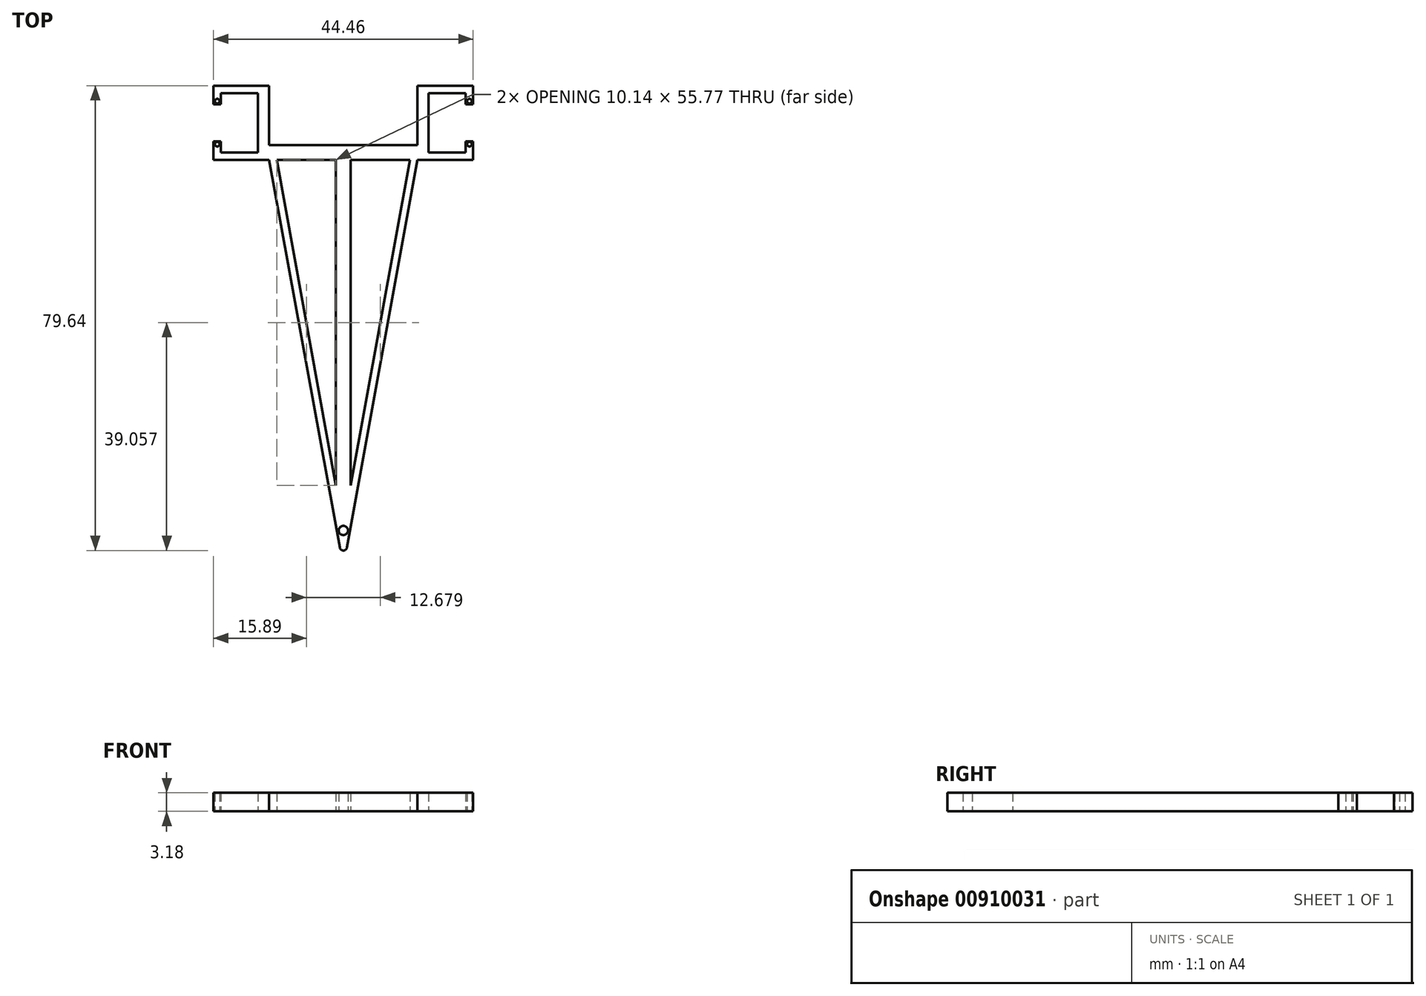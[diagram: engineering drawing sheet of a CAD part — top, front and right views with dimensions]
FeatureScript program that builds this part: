
annotation { "Feature Type Name" : "Feature", "Feature Type Description" : "" }
export const myFeature = defineFeature(function(context is Context, id is Id, definition is map)
    precondition{}
    {
        {
            var Q0;
            Q0=qCreatedBy(makeId("Top.planeOp"),FACE);
            var sketch = newSketch(context, id + "F0", { "sketchPlane" : qUnion([Q0])});
            skLineSegment(sketch, "E0", {"start": v(-22.23, 11.43) * mm, "end": v(-12.7, 11.43) * mm});
            skLineSegment(sketch, "E1", {"start": v(-12.7, 11.43) * mm, "end": v(-12.7, -1.27) * mm});
            skLineSegment(sketch, "E2", {"start": v(-12.7, -1.27) * mm, "end": v(-22.23, -1.27) * mm});
            skLineSegment(sketch, "E3", {"start": v(-22.23, -1.27) * mm, "end": v(-22.23, 1.9) * mm});
            skLineSegment(sketch, "E4", {"start": v(-22.23, 1.9) * mm, "end": v(-20.96, 1.9) * mm});
            skLineSegment(sketch, "E5", {"start": v(-20.96, 1.9) * mm, "end": v(-20.96, 0) * mm});
            skLineSegment(sketch, "E6", {"start": v(-20.96, 0) * mm, "end": v(-14.6, 0) * mm});
            skLineSegment(sketch, "E7", {"start": v(-14.6, 0) * mm, "end": v(-14.6, 10.16) * mm});
            skLineSegment(sketch, "E8", {"start": v(-14.6, 10.16) * mm, "end": v(-20.96, 10.16) * mm});
            skLineSegment(sketch, "E9", {"start": v(-20.96, 10.16) * mm, "end": v(-20.96, 8.26) * mm});
            skLineSegment(sketch, "E10", {"start": v(-20.96, 8.25) * mm, "end": v(-22.23, 8.25) * mm});
            skLineSegment(sketch, "E11", {"start": v(-22.23, 8.26) * mm, "end": v(-22.23, 11.43) * mm});
            skLineSegment(sketch, "E12.MirrorCS", {"start": v(14.6, 0) * mm, "end": v(14.6, 10.16) * mm});
            skLineSegment(sketch, "E13.MirrorCS", {"start": v(12.7, 11.43) * mm, "end": v(12.7, -1.27) * mm});
            skLineSegment(sketch, "E14.MirrorCS", {"start": v(20.96, 0) * mm, "end": v(14.6, 0) * mm});
            skLineSegment(sketch, "E15.MirrorCS", {"start": v(12.7, -1.27) * mm, "end": v(22.23, -1.27) * mm});
            skLineSegment(sketch, "E16.MirrorCS", {"start": v(22.23, -1.27) * mm, "end": v(22.23, 1.9) * mm});
            skLineSegment(sketch, "E17.MirrorCS", {"start": v(20.96, 1.9) * mm, "end": v(20.96, 0) * mm});
            skLineSegment(sketch, "E18.MirrorCS", {"start": v(22.23, 1.9) * mm, "end": v(20.96, 1.9) * mm});
            skLineSegment(sketch, "E19.MirrorCS", {"start": v(20.96, 8.25) * mm, "end": v(22.23, 8.25) * mm});
            skLineSegment(sketch, "E20.MirrorCS", {"start": v(22.23, 8.26) * mm, "end": v(22.23, 11.43) * mm});
            skLineSegment(sketch, "E21.MirrorCS", {"start": v(20.96, 10.16) * mm, "end": v(20.96, 8.26) * mm});
            skLineSegment(sketch, "E22.MirrorCS", {"start": v(14.6, 10.16) * mm, "end": v(20.96, 10.16) * mm});
            skLineSegment(sketch, "E23.MirrorCS", {"start": v(22.23, 11.43) * mm, "end": v(12.7, 11.43) * mm});
            skCircle(sketch, "E24", {"center": v(-21.6, 8.76) * mm, "radius": 0.4 * mm});
            skCircle(sketch, "E25", {"center": v(-21.6, 1.4) * mm, "radius": 0.4 * mm});
            skCircle(sketch, "E26.MirrorC", {"center": v(21.6, 8.76) * mm, "radius": 0.4 * mm});
            skCircle(sketch, "E27.MirrorC", {"center": v(21.6, 1.4) * mm, "radius": 0.4 * mm});
            skLineSegment(sketch, "E28", {"start": v(-12.7, 1.27) * mm, "end": v(12.7, 1.27) * mm});
            skLineSegment(sketch, "E29", {"start": v(-12.7, -1.27) * mm, "end": v(12.7, -1.27) * mm});
            skLineSegment(sketch, "E30", {"start": v(-12.7, -1.27) * mm, "end": v(-0.62, -67.68) * mm});
            skLineSegment(sketch, "E31", {"start": v(0.62, -67.68) * mm, "end": v(12.7, -1.27) * mm});
            skLineSegment(sketch, "E32", {"start": v(11.4, -1.27) * mm, "end": v(0, -64.02) * mm});
            skLineSegment(sketch, "E33", {"start": v(0, -64.02) * mm, "end": v(-11.4, -1.27) * mm});
            skLineSegment(sketch, "E34", {"start": v(1.27, -57.04) * mm, "end": v(1.27, -1.27) * mm});
            skLineSegment(sketch, "E35", {"start": v(-1.27, -1.27) * mm, "end": v(-1.27, -57.04) * mm});
            skLineSegment(sketch, "E36", {"start": v(1.27, -57.04) * mm, "end": v(-1.27, -57.04) * mm});
            skCircle(sketch, "E37", {"center": v(0, -64.77) * mm, "radius": 0.8 * mm});
            skPoint(sketch, "E38.visualSharp", {"position": v(0, -71.12) * mm});
            skArc(sketch, "E39.filletArc", {"start": v(-0.62, -67.68) * mm, "mid": v(0, -68.2) * mm, "end": v(0.62, -67.68) * mm});
            skSolve(sketch);
        }
        {
            var Q0;
            {var subQ0=sQuery(id+"F0.wireOp",EDGE,"E0");Q0=makeQuery(id+"F0.imprint","IMPRINT",FACE,{"disambiguationData":[TD([[makeQuery(id+"F0.imprint","IMPRINT",EDGE,{"derivedFrom":subQ0}),-1.0]])]});}
            var Q1;
            {var subQ4=sQuery(id+"F0.wireOp",EDGE,"E28");Q1=makeQuery(id+"F0.imprint","IMPRINT",FACE,{"disambiguationData":[TD([[makeQuery(id+"F0.imprint","IMPRINT",EDGE,{"derivedFrom":subQ4}),-1.0]])]});}
            var Q2;
            Q2=makeQuery(id+"F0.imprint","IMPRINT",FACE,{"disambiguationData":[TD([[makeQuery(id+"F0.imprint","IMPRINT",EDGE,{"derivedFrom":sQuery(id+"F0.wireOp",EDGE,"E12.MirrorCS")}),1.0]])]});
            var Q3;
            {var subQ8=sQuery(id+"F0.wireOp",EDGE,"E30");Q3=makeQuery(id+"F0.imprint","IMPRINT",FACE,{"disambiguationData":[TD([[makeQuery(id+"F0.imprint","IMPRINT",EDGE,{"derivedFrom":subQ8}),1.0]])]});}
            var Q4;
            {var subQ0=sQuery(id+"F0.wireOp",EDGE,"E34");Q4=makeQuery(id+"F0.imprint","IMPRINT",FACE,{"disambiguationData":[TD([[makeQuery(id+"F0.imprint","IMPRINT",EDGE,{"derivedFrom":subQ0}),1.0]])]});}
            var Q5;
            {var subQ0=sQuery(id+"F0.wireOp",EDGE,"E36");Q5=makeQuery(id+"F0.imprint","IMPRINT",FACE,{"disambiguationData":[TD([[makeQuery(id+"F0.imprint","IMPRINT",EDGE,{"derivedFrom":subQ0}),1.0]])]});}
            extrude(context, id + "F1", {"entities" : qUnion([Q0, Q1, Q2, Q3, Q4, Q5]), "depth" : 3.17 * mm, "offsetDistance" : 25.4 * mm});
        }
    });
